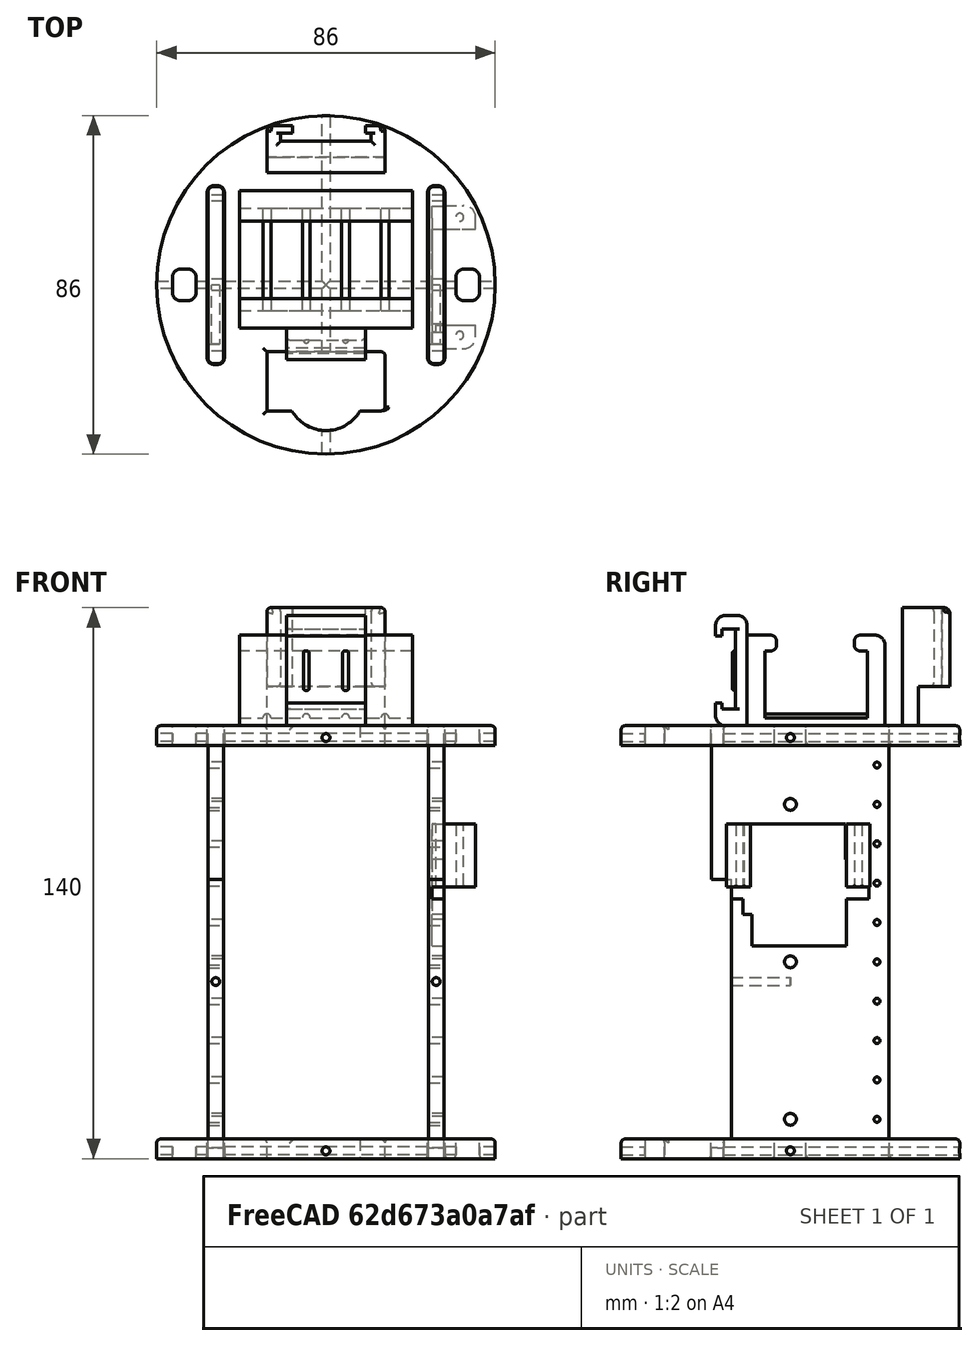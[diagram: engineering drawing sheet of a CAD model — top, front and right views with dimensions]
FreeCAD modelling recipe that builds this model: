
FCSTD DOCUMENT  (FreeCAD 1.0R39109 (Git))
Label: LateralIzquierdo_Capsula
License: All rights reserved
LicenseURL: http://en.wikipedia.org/wiki/All_rights_reserved
objects: Part::Cut×130, Part::Cylinder×98, Part::Fillet×96, Part::Box×72, Part::MultiFuse×37, Part::Offset×12, Part::Chamfer×1
note: 446 computed .brp shape members not serialized (recipe doc carries the construction recipe); baked Part::Feature solids carry a one-line shape summary decoded from their .brp

FEATURE [Part::Box] Box  label="Extensor"
  AttacherType = Attacher::AttachEngine3D
  Height = 66
  Length = 11
  Placement = pos=(30,-28,3) rot=(0,0,1;1.5708rad)
  Width = 60
FEATURE [Part::Box] Box001  label="Cubo001"
  AttacherType = Attacher::AttachEngine3D
  Height = 110
  Length = 45
  Placement = pos=(-30,25,0) rot=(0,0,-1;1.5708rad)
  Width = 4
FEATURE [Part::Box] Box002  label="Cubo002"
  AttacherType = Attacher::AttachEngine3D
  Height = 110
  Length = 45
  Placement = pos=(-30,25,0) rot=(0,0,-1;1.5708rad)
  Width = 4
FEATURE [Part::Box] Box003  label="Cubo003"
  AttacherType = Attacher::AttachEngine3D
  Height = 10
  Length = 30
  Placement = pos=(-15,-32,0) rot=(0,0,1;0rad)
  Width = 15
FEATURE [Part::Box] Box005  label="Cubo004"
  AttacherType = Attacher::AttachEngine3D
  Height = 15
  Length = 26
  Placement = pos=(-13,-23,110) rot=(0,0,1;0rad)
  Width = 35
FEATURE [Part::Box] Box006  label="Cubo005"
  AttacherType = Attacher::AttachEngine3D
  Height = 150
  Length = 6
  Width = 8
FEATURE [Part::Box] Box007  label="Cubo006"
  AttacherType = Attacher::AttachEngine3D
  Height = 150
  Length = 6
  Width = 8
FEATURE [Part::Box] Box008  label="Cubo007"
  AttacherType = Attacher::AttachEngine3D
  Height = 150
  Length = 6
  Width = 8
FEATURE [Part::Box] Box009  label="Cubo008"
  AttacherType = Attacher::AttachEngine3D
  Height = 150
  Length = 6
  Width = 8
FEATURE [Part::Box] Box010  label="Cubo009"
  AttacherType = Attacher::AttachEngine3D
  Height = 11.6
  Length = 20.8
  Placement = pos=(-10.5,-23,110) rot=(0,0,1;0rad)
  Width = 35
FEATURE [Part::Box] Box011  label="Cubo010"
  AttacherType = Attacher::AttachEngine3D
  Height = 11.6
  Length = 16
  Placement = pos=(-8,-23,116) rot=(0,0,1;0rad)
  Width = 35
FEATURE [Part::Box] Box095  label="Cubo095"
  AttacherType = Attacher::AttachEngine3D
  Height = 110
  Length = 45
  Placement = pos=(-30,25,0) rot=(0,0,-1;1.5708rad)
  Width = 4
FEATURE [Part::Box] Box096  label="Cubo096"
  AttacherType = Attacher::AttachEngine3D
  Height = 110
  Length = 45
  Placement = pos=(-30,25,0) rot=(0,0,-1;1.5708rad)
  Width = 4
FEATURE [Part::Box] Box097  label="Cubo097"
  AttacherType = Attacher::AttachEngine3D
  Height = 23
  Length = 24
  Width = 14
FEATURE [Part::Box] Box098  label="Cubo098"
  AttacherType = Attacher::AttachEngine3D
  Height = 3
  Length = 33.5
  Placement = pos=(-5,0,16) rot=(0,0,1;0rad)
  Width = 14
FEATURE [Part::Box] Box099  label="Cubo099"
  AttacherType = Attacher::AttachEngine3D
  Height = 1.4
  Length = 13
  Placement = pos=(9.8,5,28.6) rot=(0,0,1;0rad)
  Width = 4
FEATURE [Part::Box] Box100  label="Cubo100"
  AttacherType = Attacher::AttachEngine3D
  Height = 16
  Length = 10
  Placement = pos=(28,12.2,69) rot=(0,0,1;0rad)
  Width = 6
FEATURE [Part::Box] Box101  label="Cubo101"
  AttacherType = Attacher::AttachEngine3D
  Height = 16
  Length = 10
  Placement = pos=(28,-18.2,69) rot=(0,0,1;0rad)
  Width = 6
FEATURE [Part::Box] Box102  label="Extensor001"
  AttacherType = Attacher::AttachEngine3D
  Height = 66
  Length = 11
  Placement = pos=(30,-28,3) rot=(0,0,1;1.5708rad)
  Width = 60
FEATURE [Part::Box] Box104  label="Cubo102"
  AttacherType = Attacher::AttachEngine3D
  Height = 8
  Length = 20
  Width = 28
FEATURE [Part::Box] Box105  label="Cubo103"
  AttacherType = Attacher::AttachEngine3D
  Height = 2
  Length = 20.5
  Placement = pos=(0,4,4) rot=(0,0,1;0rad)
  Width = 20.5
FEATURE [Part::Box] Box106  label="Cubo104"
  AttacherType = Attacher::AttachEngine3D
  Height = 4
  Length = 20.5
  Placement = pos=(0,5,5) rot=(0,0,1;0rad)
  Width = 18.5
FEATURE [Part::Box] Box107  label="Cubo105"
  AttacherType = Attacher::AttachEngine3D
  Height = 8
  Length = 20
  Width = 30
FEATURE [Part::Box] Box108  label="Cubo106"
  AttacherType = Attacher::AttachEngine3D
  Height = 2
  Length = 20.5
  Placement = pos=(0,3.5,4) rot=(0,0,1;0rad)
  Width = 23
FEATURE [Part::Box] Box109  label="Cubo107"
  AttacherType = Attacher::AttachEngine3D
  Height = 4
  Length = 20.5
  Placement = pos=(0,5,5) rot=(0,0,1;0rad)
  Width = 18.5
FEATURE [Part::Box] Box110  label="Cubo108"
  AttacherType = Attacher::AttachEngine3D
  Height = 10
  Length = 20
  Placement = pos=(-9,-38,105) rot=(0,0,1;0rad)
  Width = 15
FEATURE [Part::Box] Box111  label="Cubo109"
  AttacherType = Attacher::AttachEngine3D
  Height = 110
  Length = 45
  Placement = pos=(-30,25,0) rot=(0,0,-1;1.5708rad)
  Width = 4
FEATURE [Part::Box] Box112  label="Extensor003"
  AttacherType = Attacher::AttachEngine3D
  Height = 66
  Length = 11
  Placement = pos=(30,-28,3) rot=(0,0,1;1.5708rad)
  Width = 60
FEATURE [Part::Box] Box113  label="Extensor004"
  AttacherType = Attacher::AttachEngine3D
  Height = 66
  Length = 11
  Placement = pos=(30,-28,3) rot=(0,0,1;1.5708rad)
  Width = 60
FEATURE [Part::Box] Box114  label="Cubo110"
  AttacherType = Attacher::AttachEngine3D
  Height = 110
  Length = 45
  Placement = pos=(-30,25,0) rot=(0,0,-1;1.5708rad)
  Width = 4
FEATURE [Part::Box] Box115  label="Cubo111"
  AttacherType = Attacher::AttachEngine3D
  Height = 23
  Length = 24
  Width = 14
FEATURE [Part::Box] Box116  label="Cubo112"
  AttacherType = Attacher::AttachEngine3D
  Height = 3
  Length = 33.5
  Placement = pos=(-5,0,16) rot=(0,0,1;0rad)
  Width = 14
FEATURE [Part::Box] Box117  label="Cubo113"
  AttacherType = Attacher::AttachEngine3D
  Height = 1.4
  Length = 13
  Placement = pos=(9.8,5,28.6) rot=(0,0,1;0rad)
  Width = 4
FEATURE [Part::Box] Box118  label="Cubo114"
  AttacherType = Attacher::AttachEngine3D
  Height = 16
  Length = 10
  Placement = pos=(28,12.2,69) rot=(0,0,1;0rad)
  Width = 6
FEATURE [Part::Box] Box119  label="Cubo115"
  AttacherType = Attacher::AttachEngine3D
  Height = 16
  Length = 10
  Placement = pos=(28,-18.2,69) rot=(0,0,1;0rad)
  Width = 6
FEATURE [Part::Box] Box120  label="Cubo116"
  AttacherType = Attacher::AttachEngine3D
  Height = 10
  Length = 4
  Placement = pos=(-30,-20,0) rot=(0,0,1;0rad)
  Width = 45
FEATURE [Part::Box] Box121  label="Cubo117"
  AttacherType = Attacher::AttachEngine3D
  Height = 10
  Length = 4
  Placement = pos=(-30,-20,0) rot=(0,0,1;0rad)
  Width = 45
FEATURE [Part::Box] Box122  label="Cubo118"
  AttacherType = Attacher::AttachEngine3D
  Height = 8
  Length = 20
  Width = 30
FEATURE [Part::Box] Box123  label="Cubo119"
  AttacherType = Attacher::AttachEngine3D
  Height = 2
  Length = 20.5
  Placement = pos=(0,3.5,4) rot=(0,0,1;0rad)
  Width = 23
FEATURE [Part::Box] Box124  label="Cubo120"
  AttacherType = Attacher::AttachEngine3D
  Height = 4
  Length = 20.5
  Placement = pos=(0,5,5) rot=(0,0,1;0rad)
  Width = 18.5
FEATURE [Part::Box] Box128  label="Cubo124"
  AttacherType = Attacher::AttachEngine3D
  Height = 30
  Length = 33
  Placement = pos=(-16,-43,115) rot=(0,0,1;0rad)
  Width = 30
FEATURE [Part::Box] Box129  label="Cubo125"
  AttacherType = Attacher::AttachEngine3D
  Height = 30
  Length = 33
  Placement = pos=(-16,13,110) rot=(0,0,1;0rad)
  Width = 30
FEATURE [Part::Box] Box130  label="Cubo126"
  AttacherType = Attacher::AttachEngine3D
  Height = 30
  Length = 30
  Placement = pos=(-16,13,110) rot=(0,0,1;0rad)
  Width = 4
FEATURE [Part::Box] Box131  label="Cubo127"
  AttacherType = Attacher::AttachEngine3D
  Height = 3.4
  Length = 21
  Placement = pos=(0,4.2,3) rot=(0,0,1;0rad)
  Width = 20.4
FEATURE [Part::Box] Box132  label="Cubo128"
  AttacherType = Attacher::AttachEngine3D
  Height = 4
  Length = 21
  Placement = pos=(0,5.75,6) rot=(0,0,1;0rad)
  Width = 17
FEATURE [Part::Box] Box133  label="Cubo129"
  AttacherType = Attacher::AttachEngine3D
  Height = 8
  Length = 20
  Width = 28
FEATURE [Part::Box] Box134  label="Cubo130"
  AttacherType = Attacher::AttachEngine3D
  Height = 16
  Length = 37
  Placement = pos=(-19,-15,110) rot=(0,0,1;0rad)
  Width = 30
FEATURE [Part::Box] Box135  label="Pila_ext"
  AttacherType = Attacher::AttachEngine3D
  Height = 25
  Length = 44
  Placement = pos=(-22,-11,110) rot=(0,0,1;0rad)
  Width = 35
FEATURE [Part::Box] Box136  label="Pila_int"
  AttacherType = Attacher::AttachEngine3D
  Height = 17
  Length = 44
  Placement = pos=(-22,-6.5,114) rot=(0,0,1;0rad)
  Width = 26
FEATURE [Part::Box] Box137  label="hueco_pila"
  AttacherType = Attacher::AttachEngine3D
  Height = 16.65
  Length = 44
  Placement = pos=(-22,-3.5,122) rot=(0,0,1;0rad)
  Width = 19.72
FEATURE [Part::Box] Box165  label="Cubo155"
  AttacherType = Attacher::AttachEngine3D
  Height = 17
  Length = 19
  Placement = pos=(27,-9.8,59) rot=(0,0,1;0rad)
  Width = 24
FEATURE [Part::Box] Box166  label="Cubo156"
  AttacherType = Attacher::AttachEngine3D
  Height = 66
  Length = 60
  Placement = pos=(-30,-20,5) rot=(0,0,1;0rad)
  Width = 5
FEATURE [Part::Box] Box167  label="Cubo157"
  AttacherType = Attacher::AttachEngine3D
  Height = 66
  Length = 60
  Placement = pos=(-30,-20,5) rot=(0,0,1;0rad)
  Width = 5
FEATURE [Part::Box] Box168  label="Cubo158"
  AttacherType = Attacher::AttachEngine3D
  Height = 3
  Length = 4
  Placement = pos=(27,7,66) rot=(0,0,1;0rad)
  Width = 13
FEATURE [Part::Box] Box169  label="Cubo159"
  AttacherType = Attacher::AttachEngine3D
  Height = 3
  Length = 4
  Placement = pos=(27,-9.8,56) rot=(0,0,1;0rad)
  Width = 24
FEATURE [Part::Box] Box170  label="Cubo160"
  AttacherType = Attacher::AttachEngine3D
  Height = 10
  Length = 30
  Placement = pos=(-15,-32,0) rot=(0,0,1;0rad)
  Width = 15
FEATURE [Part::Box] Box171  label="Cubo161"
  AttacherType = Attacher::AttachEngine3D
  Height = 150
  Length = 6
  Width = 8
FEATURE [Part::Box] Box172  label="Cubo162"
  AttacherType = Attacher::AttachEngine3D
  Height = 150
  Length = 6
  Width = 8
FEATURE [Part::Box] Box173  label="Cubo163"
  AttacherType = Attacher::AttachEngine3D
  Height = 110
  Length = 45
  Placement = pos=(-30,25,0) rot=(0,0,-1;1.5708rad)
  Width = 4
FEATURE [Part::Box] Box174  label="Extensor005"
  AttacherType = Attacher::AttachEngine3D
  Height = 66
  Length = 11
  Placement = pos=(30,-28,3) rot=(0,0,1;1.5708rad)
  Width = 60
FEATURE [Part::Box] Box175  label="Extensor006"
  AttacherType = Attacher::AttachEngine3D
  Height = 66
  Length = 11
  Placement = pos=(30,-28,3) rot=(0,0,1;1.5708rad)
  Width = 60
FEATURE [Part::Box] Box176  label="Cubo164"
  AttacherType = Attacher::AttachEngine3D
  Height = 110
  Length = 45
  Placement = pos=(-30,25,0) rot=(0,0,-1;1.5708rad)
  Width = 4
FEATURE [Part::Box] Box177  label="Cubo165"
  AttacherType = Attacher::AttachEngine3D
  Height = 23
  Length = 24
  Width = 14
FEATURE [Part::Box] Box178  label="Cubo166"
  AttacherType = Attacher::AttachEngine3D
  Height = 3
  Length = 33.5
  Placement = pos=(-5,0,16) rot=(0,0,1;0rad)
  Width = 14
FEATURE [Part::Box] Box179  label="Cubo167"
  AttacherType = Attacher::AttachEngine3D
  Height = 1.4
  Length = 13
  Placement = pos=(9.8,5,28.6) rot=(0,0,1;0rad)
  Width = 4
FEATURE [Part::Box] Box180  label="Cubo168"
  AttacherType = Attacher::AttachEngine3D
  Height = 16
  Length = 10
  Placement = pos=(28,12.2,69) rot=(0,0,1;0rad)
  Width = 6
FEATURE [Part::Box] Box181  label="Cubo169"
  AttacherType = Attacher::AttachEngine3D
  Height = 16
  Length = 10
  Placement = pos=(28,-18.2,69) rot=(0,0,1;0rad)
  Width = 6
FEATURE [Part::Box] Box182  label="Cubo170"
  AttacherType = Attacher::AttachEngine3D
  Height = 10
  Length = 4
  Placement = pos=(-30,-20,0) rot=(0,0,1;0rad)
  Width = 45
FEATURE [Part::Box] Box183  label="Cubo171"
  AttacherType = Attacher::AttachEngine3D
  Height = 10
  Length = 4
  Placement = pos=(-30,-20,0) rot=(0,0,1;0rad)
  Width = 45
FEATURE [Part::Box] Box184  label="Cubo172"
  AttacherType = Attacher::AttachEngine3D
  Height = 10
  Length = 120
  Placement = pos=(-50,-47,100) rot=(0,0,1;0rad)
  Width = 120
FEATURE [Part::Box] Box197  label="Cubo184"
  AttacherType = Attacher::AttachEngine3D
  Height = 16
  Length = 3
  Placement = pos=(27,12,69) rot=(0,0,1;0rad)
  Width = 2
FEATURE [Part::Box] Box198  label="Cubo185"
  AttacherType = Attacher::AttachEngine3D
  Height = 24
  Length = 3
  Placement = pos=(27,14.2,54) rot=(1,0,0;1.5708rad)
  Width = 4
FEATURE [Part::Cut] Cut016
  Base = -> Box005
  Tool = -> Box010
FEATURE [Part::Cut] Cut017
  Base = -> Cut016
  Placement = pos=(-5,0,0) rot=(0,0,1;1.5708rad)
  Tool = -> Box011
FEATURE [Part::Cut] Cut115
  Base = -> Box104
  Tool = -> Box105
FEATURE [Part::Cut] Cut116
  Base = -> Cut115
  Tool = -> Box106
FEATURE [Part::Cut] Cut117
  Base = -> Box107
  Tool = -> Box108
FEATURE [Part::Cut] Cut118
  Base = -> Cut117
  Tool = -> Box109
FEATURE [Part::Cut] Cut143
  Base = -> Box122
  Tool = -> Box123
FEATURE [Part::Cut] Cut144
  Base = -> Cut143
  Tool = -> Box124
FEATURE [Part::Cut] Cut149
  Base = -> Box133
  Tool = -> Box131
FEATURE [Part::Cut] Cut150
  Base = -> Cut149
  Tool = -> Box132
FEATURE [Part::Cut] Cut152
  Base = -> Box135
  Tool = -> Box136
FEATURE [Part::Cut] Cut153  label="PortaPIlas_9V"
  Base = -> Cut152
  Placement = pos=(0,0,-2) rot=(0,0,1;0rad)
  Tool = -> Box137
FEATURE [Part::Cylinder] Cylinder  label="Cilindro"
  Angle = 360
  AttacherType = Attacher::AttachEngine3D
  FirstAngle = 0
  Height = 5
  Radius = 43
  SecondAngle = 0
FEATURE [Part::Cylinder] Cylinder002  label="Cilindro002"
  Angle = 360
  AttacherType = Attacher::AttachEngine3D
  FirstAngle = 0
  Height = 20
  Placement = pos=(0,44,1.5) rot=(1,0,0;1.5708rad)
  Radius = 0.5
  SecondAngle = 0
FEATURE [Part::Cylinder] Cylinder003  label="Cilindro003"
  Angle = 360
  AttacherType = Attacher::AttachEngine3D
  FirstAngle = 0
  Height = 20
  Placement = pos=(0,-26,1.5) rot=(1,0,0;1.5708rad)
  Radius = 0.5
  SecondAngle = 0
FEATURE [Part::Cylinder] Cylinder004  label="Cilindro004"
  Angle = 360
  AttacherType = Attacher::AttachEngine3D
  FirstAngle = 0
  Height = 3
  Radius = 43
  SecondAngle = 0
FEATURE [Part::Cylinder] Cylinder005  label="Cilindro005"
  Angle = 360
  AttacherType = Attacher::AttachEngine3D
  FirstAngle = 0
  Height = 20
  Placement = pos=(0,44,1.5) rot=(1,0,0;1.5708rad)
  Radius = 0.5
  SecondAngle = 0
FEATURE [Part::Cylinder] Cylinder006  label="Cilindro006"
  Angle = 360
  AttacherType = Attacher::AttachEngine3D
  FirstAngle = 0
  Height = 20
  Placement = pos=(0,-26,1.5) rot=(1,0,0;1.5708rad)
  Radius = 0.5
  SecondAngle = 0
FEATURE [Part::Cylinder] Cylinder008  label="Cilindro008"
  Angle = 360
  AttacherType = Attacher::AttachEngine3D
  FirstAngle = 0
  Height = 100
  Placement = pos=(-46,0,50) rot=(0,1,0;1.5708rad)
  Radius = 1.5
  SecondAngle = 0
FEATURE [Part::Cylinder] Cylinder009  label="Cilindro009"
  Angle = 360
  AttacherType = Attacher::AttachEngine3D
  FirstAngle = 0
  Height = 100
  Placement = pos=(-46,0,90) rot=(0,1,0;1.5708rad)
  Radius = 1.5
  SecondAngle = 0
FEATURE [Part::Cylinder] Cylinder010  label="Cilindro010"
  Angle = 360
  AttacherType = Attacher::AttachEngine3D
  FirstAngle = 0
  Height = 100
  Placement = pos=(-46,0,10) rot=(0,1,0;1.5708rad)
  Radius = 1.5
  SecondAngle = 0
FEATURE [Part::Cylinder] Cylinder011  label="Cilindro011"
  Angle = 360
  AttacherType = Attacher::AttachEngine3D
  FirstAngle = 0
  Height = 10
  Placement = pos=(0,-27,0) rot=(0,0,1;0rad)
  Radius = 10
  SecondAngle = 0
FEATURE [Part::Cylinder] Cylinder071  label="Cilindro071"
  Angle = 360
  AttacherType = Attacher::AttachEngine3D
  FirstAngle = 0
  Height = 100
  Placement = pos=(-46,0,50) rot=(0,1,0;1.5708rad)
  Radius = 1.5
  SecondAngle = 0
FEATURE [Part::Cylinder] Cylinder072  label="Cilindro072"
  Angle = 360
  AttacherType = Attacher::AttachEngine3D
  FirstAngle = 0
  Height = 100
  Placement = pos=(-46,0,90) rot=(0,1,0;1.5708rad)
  Radius = 1.5
  SecondAngle = 0
FEATURE [Part::Cylinder] Cylinder073  label="Cilindro073"
  Angle = 360
  AttacherType = Attacher::AttachEngine3D
  FirstAngle = 0
  Height = 100
  Placement = pos=(-46,0,10) rot=(0,1,0;1.5708rad)
  Radius = 1.5
  SecondAngle = 0
FEATURE [Part::Cylinder] Cylinder074  label="Cilindro074"
  Angle = 360
  AttacherType = Attacher::AttachEngine3D
  FirstAngle = 0
  Height = 3
  Placement = pos=(7,7,23) rot=(0,0,1;0rad)
  Radius = 7
  SecondAngle = 0
FEATURE [Part::Cylinder] Cylinder075  label="Cilindro075"
  Angle = 360
  AttacherType = Attacher::AttachEngine3D
  FirstAngle = 0
  Height = 3
  Placement = pos=(14,7,23) rot=(0,0,1;0rad)
  Radius = 2
  SecondAngle = 0
FEATURE [Part::Cylinder] Cylinder076  label="Cilindro076"
  Angle = 360
  AttacherType = Attacher::AttachEngine3D
  FirstAngle = 0
  Height = 10
  Placement = pos=(-3.2,7,12) rot=(0,0,1;0rad)
  Radius = 1.65
  SecondAngle = 0
FEATURE [Part::Cylinder] Cylinder077  label="Cilindro077"
  Angle = 360
  AttacherType = Attacher::AttachEngine3D
  FirstAngle = 0
  Height = 10
  Placement = pos=(26.8,7,12) rot=(0,0,1;0rad)
  Radius = 1.65
  SecondAngle = 0
FEATURE [Part::Cylinder] Cylinder078  label="Cilindro078"
  Angle = 360
  AttacherType = Attacher::AttachEngine3D
  FirstAngle = 0
  Height = 4
  Placement = pos=(7,7,26) rot=(0,0,1;0rad)
  Radius = 3.5
  SecondAngle = 0
FEATURE [Part::Cylinder] Cylinder079  label="Cilindro079"
  Angle = 360
  AttacherType = Attacher::AttachEngine3D
  FirstAngle = 0
  Height = 10
  Placement = pos=(21,7,25) rot=(0,0,1;0rad)
  Radius = 0.25
  SecondAngle = 0
FEATURE [Part::Cylinder] Cylinder080  label="Cilindro080"
  Angle = 360
  AttacherType = Attacher::AttachEngine3D
  FirstAngle = 0
  Height = 10
  Placement = pos=(19,7,25) rot=(0,0,1;0rad)
  Radius = 0.25
  SecondAngle = 0
FEATURE [Part::Cylinder] Cylinder081  label="Cilindro081"
  Angle = 360
  AttacherType = Attacher::AttachEngine3D
  FirstAngle = 0
  Height = 10
  Placement = pos=(17,7,25) rot=(0,0,1;0rad)
  Radius = 0.25
  SecondAngle = 0
FEATURE [Part::Cylinder] Cylinder082  label="Cilindro082"
  Angle = 360
  AttacherType = Attacher::AttachEngine3D
  FirstAngle = 0
  Height = 10
  Placement = pos=(15,7,27) rot=(0,0,1;0rad)
  Radius = 0.25
  SecondAngle = 0
FEATURE [Part::Cylinder] Cylinder083  label="Cilindro083"
  Angle = 360
  AttacherType = Attacher::AttachEngine3D
  FirstAngle = 0
  Height = 10
  Placement = pos=(13,7,27) rot=(0,0,1;0rad)
  Radius = 0.25
  SecondAngle = 0
FEATURE [Part::Cylinder] Cylinder084  label="Cilindro084"
  Angle = 360
  AttacherType = Attacher::AttachEngine3D
  FirstAngle = 0
  Height = 20
  Placement = pos=(34,-14.8,66) rot=(0,0,1;0rad)
  Radius = 1
  SecondAngle = 0
FEATURE [Part::Cylinder] Cylinder085  label="Cilindro085"
  Angle = 360
  AttacherType = Attacher::AttachEngine3D
  FirstAngle = 0
  Height = 20
  Placement = pos=(34,15.2,66) rot=(0,0,1;0rad)
  Radius = 1
  SecondAngle = 0
FEATURE [Part::Cylinder] Cylinder086  label="Cilindro086"
  Angle = 360
  AttacherType = Attacher::AttachEngine3D
  FirstAngle = 0
  Height = 100
  Placement = pos=(-46,0,50) rot=(0,1,0;1.5708rad)
  Radius = 1.5
  SecondAngle = 0
FEATURE [Part::Cylinder] Cylinder087  label="Cilindro087"
  Angle = 360
  AttacherType = Attacher::AttachEngine3D
  FirstAngle = 0
  Height = 100
  Placement = pos=(-46,0,90) rot=(0,1,0;1.5708rad)
  Radius = 1.5
  SecondAngle = 0
FEATURE [Part::Cylinder] Cylinder088  label="Cilindro088"
  Angle = 360
  AttacherType = Attacher::AttachEngine3D
  FirstAngle = 0
  Height = 100
  Placement = pos=(-46,0,10) rot=(0,1,0;1.5708rad)
  Radius = 1.5
  SecondAngle = 0
FEATURE [Part::Cylinder] Cylinder089  label="Cilindro089"
  Angle = 360
  AttacherType = Attacher::AttachEngine3D
  FirstAngle = 0
  Height = 100
  Placement = pos=(-46,0,50) rot=(0,1,0;1.5708rad)
  Radius = 1.5
  SecondAngle = 0
FEATURE [Part::Cylinder] Cylinder090  label="Cilindro090"
  Angle = 360
  AttacherType = Attacher::AttachEngine3D
  FirstAngle = 0
  Height = 100
  Placement = pos=(-46,0,90) rot=(0,1,0;1.5708rad)
  Radius = 1.5
  SecondAngle = 0
FEATURE [Part::Cylinder] Cylinder091  label="Cilindro091"
  Angle = 360
  AttacherType = Attacher::AttachEngine3D
  FirstAngle = 0
  Height = 100
  Placement = pos=(-46,0,10) rot=(0,1,0;1.5708rad)
  Radius = 1.5
  SecondAngle = 0
FEATURE [Part::Cylinder] Cylinder092  label="Cilindro092"
  Angle = 360
  AttacherType = Attacher::AttachEngine3D
  FirstAngle = 0
  Height = 3
  Placement = pos=(7,7,23) rot=(0,0,1;0rad)
  Radius = 7
  SecondAngle = 0
FEATURE [Part::Cylinder] Cylinder093  label="Cilindro093"
  Angle = 360
  AttacherType = Attacher::AttachEngine3D
  FirstAngle = 0
  Height = 3
  Placement = pos=(14,7,23) rot=(0,0,1;0rad)
  Radius = 2
  SecondAngle = 0
FEATURE [Part::Cylinder] Cylinder094  label="Cilindro094"
  Angle = 360
  AttacherType = Attacher::AttachEngine3D
  FirstAngle = 0
  Height = 10
  Placement = pos=(-3.2,7,12) rot=(0,0,1;0rad)
  Radius = 1.65
  SecondAngle = 0
FEATURE [Part::Cylinder] Cylinder095  label="Cilindro095"
  Angle = 360
  AttacherType = Attacher::AttachEngine3D
  FirstAngle = 0
  Height = 10
  Placement = pos=(26.8,7,12) rot=(0,0,1;0rad)
  Radius = 1.65
  SecondAngle = 0
FEATURE [Part::Cylinder] Cylinder096  label="Cilindro096"
  Angle = 360
  AttacherType = Attacher::AttachEngine3D
  FirstAngle = 0
  Height = 4
  Placement = pos=(7,7,26) rot=(0,0,1;0rad)
  Radius = 3.5
  SecondAngle = 0
FEATURE [Part::Cylinder] Cylinder097  label="Cilindro097"
  Angle = 360
  AttacherType = Attacher::AttachEngine3D
  FirstAngle = 0
  Height = 10
  Placement = pos=(21,7,25) rot=(0,0,1;0rad)
  Radius = 0.25
  SecondAngle = 0
FEATURE [Part::Cylinder] Cylinder098  label="Cilindro098"
  Angle = 360
  AttacherType = Attacher::AttachEngine3D
  FirstAngle = 0
  Height = 10
  Placement = pos=(19,7,25) rot=(0,0,1;0rad)
  Radius = 0.25
  SecondAngle = 0
FEATURE [Part::Cylinder] Cylinder099  label="Cilindro099"
  Angle = 360
  AttacherType = Attacher::AttachEngine3D
  FirstAngle = 0
  Height = 10
  Placement = pos=(17,7,25) rot=(0,0,1;0rad)
  Radius = 0.25
  SecondAngle = 0
FEATURE [Part::Cylinder] Cylinder100  label="Cilindro100"
  Angle = 360
  AttacherType = Attacher::AttachEngine3D
  FirstAngle = 0
  Height = 10
  Placement = pos=(15,7,27) rot=(0,0,1;0rad)
  Radius = 0.25
  SecondAngle = 0
FEATURE [Part::Cylinder] Cylinder101  label="Cilindro101"
  Angle = 360
  AttacherType = Attacher::AttachEngine3D
  FirstAngle = 0
  Height = 10
  Placement = pos=(13,7,27) rot=(0,0,1;0rad)
  Radius = 0.25
  SecondAngle = 0
FEATURE [Part::Cylinder] Cylinder102  label="Cilindro102"
  Angle = 360
  AttacherType = Attacher::AttachEngine3D
  FirstAngle = 0
  Height = 20
  Placement = pos=(34,-14.8,66) rot=(0,0,1;0rad)
  Radius = 1
  SecondAngle = 0
FEATURE [Part::Cylinder] Cylinder103  label="Cilindro103"
  Angle = 360
  AttacherType = Attacher::AttachEngine3D
  FirstAngle = 0
  Height = 20
  Placement = pos=(34,15.2,66) rot=(0,0,1;0rad)
  Radius = 1
  SecondAngle = 0
FEATURE [Part::Cylinder] Cylinder104  label="Cilindro104"
  Angle = 360
  AttacherType = Attacher::AttachEngine3D
  FirstAngle = 0
  Height = 100
  Placement = pos=(0,52,2) rot=(1,0,0;1.5708rad)
  Radius = 1
  SecondAngle = 0
FEATURE [Part::Cylinder] Cylinder109  label="Cilindro109"
  Angle = 360
  AttacherType = Attacher::AttachEngine3D
  FirstAngle = 0
  Height = 15
  Placement = pos=(-28,0,45) rot=(1,0,0;1.5708rad)
  Radius = 1
  SecondAngle = 0
FEATURE [Part::Cylinder] Cylinder110  label="Cilindro110"
  Angle = 360
  AttacherType = Attacher::AttachEngine3D
  FirstAngle = 0
  Height = 15
  Placement = pos=(28,0,45) rot=(1,0,0;1.5708rad)
  Radius = 1
  SecondAngle = 0
FEATURE [Part::Cylinder] Cylinder111  label="Cilindro111"
  Angle = 360
  AttacherType = Attacher::AttachEngine3D
  FirstAngle = 0
  Height = 67
  Placement = pos=(-33,22,10) rot=(0,1,0;1.5708rad)
  Radius = 0.75
  SecondAngle = 0
FEATURE [Part::Cylinder] Cylinder112  label="Cilindro112"
  Angle = 360
  AttacherType = Attacher::AttachEngine3D
  FirstAngle = 0
  Height = 67
  Placement = pos=(-33,22,100) rot=(0,1,0;1.5708rad)
  Radius = 0.75
  SecondAngle = 0
FEATURE [Part::Cylinder] Cylinder113  label="Cilindro113"
  Angle = 360
  AttacherType = Attacher::AttachEngine3D
  FirstAngle = 0
  Height = 67
  Placement = pos=(-33,22,20) rot=(0,1,0;1.5708rad)
  Radius = 0.75
  SecondAngle = 0
FEATURE [Part::Cylinder] Cylinder114  label="Cilindro114"
  Angle = 360
  AttacherType = Attacher::AttachEngine3D
  FirstAngle = 0
  Height = 67
  Placement = pos=(-33,22,30) rot=(0,1,0;1.5708rad)
  Radius = 0.75
  SecondAngle = 0
FEATURE [Part::Cylinder] Cylinder115  label="Cilindro115"
  Angle = 360
  AttacherType = Attacher::AttachEngine3D
  FirstAngle = 0
  Height = 67
  Placement = pos=(-33,22,40) rot=(0,1,0;1.5708rad)
  Radius = 0.75
  SecondAngle = 0
FEATURE [Part::Cylinder] Cylinder116  label="Cilindro116"
  Angle = 360
  AttacherType = Attacher::AttachEngine3D
  FirstAngle = 0
  Height = 67
  Placement = pos=(-33,22,50) rot=(0,1,0;1.5708rad)
  Radius = 0.75
  SecondAngle = 0
FEATURE [Part::Cylinder] Cylinder117  label="Cilindro117"
  Angle = 360
  AttacherType = Attacher::AttachEngine3D
  FirstAngle = 0
  Height = 67
  Placement = pos=(-33,22,60) rot=(0,1,0;1.5708rad)
  Radius = 0.75
  SecondAngle = 0
FEATURE [Part::Cylinder] Cylinder118  label="Cilindro118"
  Angle = 360
  AttacherType = Attacher::AttachEngine3D
  FirstAngle = 0
  Height = 67
  Placement = pos=(-33,22,70) rot=(0,1,0;1.5708rad)
  Radius = 0.75
  SecondAngle = 0
FEATURE [Part::Cylinder] Cylinder119  label="Cilindro119"
  Angle = 360
  AttacherType = Attacher::AttachEngine3D
  FirstAngle = 0
  Height = 67
  Placement = pos=(-33,22,80) rot=(0,1,0;1.5708rad)
  Radius = 0.75
  SecondAngle = 0
FEATURE [Part::Cylinder] Cylinder120  label="Cilindro120"
  Angle = 360
  AttacherType = Attacher::AttachEngine3D
  FirstAngle = 0
  Height = 67
  Placement = pos=(-33,22,90) rot=(0,1,0;1.5708rad)
  Radius = 0.75
  SecondAngle = 0
FEATURE [Part::Cylinder] Cylinder121  label="Cilindro121"
  Angle = 360
  AttacherType = Attacher::AttachEngine3D
  FirstAngle = 0
  Height = 67
  Placement = pos=(-33,22,10) rot=(0,1,0;1.5708rad)
  Radius = 0.75
  SecondAngle = 0
FEATURE [Part::Cylinder] Cylinder122  label="Cilindro122"
  Angle = 360
  AttacherType = Attacher::AttachEngine3D
  FirstAngle = 0
  Height = 67
  Placement = pos=(-33,22,100) rot=(0,1,0;1.5708rad)
  Radius = 0.75
  SecondAngle = 0
FEATURE [Part::Cylinder] Cylinder123  label="Cilindro123"
  Angle = 360
  AttacherType = Attacher::AttachEngine3D
  FirstAngle = 0
  Height = 67
  Placement = pos=(-33,22,20) rot=(0,1,0;1.5708rad)
  Radius = 0.75
  SecondAngle = 0
FEATURE [Part::Cylinder] Cylinder124  label="Cilindro124"
  Angle = 360
  AttacherType = Attacher::AttachEngine3D
  FirstAngle = 0
  Height = 67
  Placement = pos=(-33,22,30) rot=(0,1,0;1.5708rad)
  Radius = 0.75
  SecondAngle = 0
FEATURE [Part::Cylinder] Cylinder125  label="Cilindro125"
  Angle = 360
  AttacherType = Attacher::AttachEngine3D
  FirstAngle = 0
  Height = 67
  Placement = pos=(-33,22,40) rot=(0,1,0;1.5708rad)
  Radius = 0.75
  SecondAngle = 0
FEATURE [Part::Cylinder] Cylinder126  label="Cilindro126"
  Angle = 360
  AttacherType = Attacher::AttachEngine3D
  FirstAngle = 0
  Height = 67
  Placement = pos=(-33,22,50) rot=(0,1,0;1.5708rad)
  Radius = 0.75
  SecondAngle = 0
FEATURE [Part::Cylinder] Cylinder127  label="Cilindro127"
  Angle = 360
  AttacherType = Attacher::AttachEngine3D
  FirstAngle = 0
  Height = 67
  Placement = pos=(-33,22,60) rot=(0,1,0;1.5708rad)
  Radius = 0.75
  SecondAngle = 0
FEATURE [Part::Cylinder] Cylinder128  label="Cilindro128"
  Angle = 360
  AttacherType = Attacher::AttachEngine3D
  FirstAngle = 0
  Height = 67
  Placement = pos=(-33,22,70) rot=(0,1,0;1.5708rad)
  Radius = 0.75
  SecondAngle = 0
FEATURE [Part::Cylinder] Cylinder129  label="Cilindro129"
  Angle = 360
  AttacherType = Attacher::AttachEngine3D
  FirstAngle = 0
  Height = 67
  Placement = pos=(-33,22,80) rot=(0,1,0;1.5708rad)
  Radius = 0.75
  SecondAngle = 0
FEATURE [Part::Cylinder] Cylinder130  label="Cilindro130"
  Angle = 360
  AttacherType = Attacher::AttachEngine3D
  FirstAngle = 0
  Height = 67
  Placement = pos=(-33,22,90) rot=(0,1,0;1.5708rad)
  Radius = 0.75
  SecondAngle = 0
FEATURE [Part::Cylinder] Cylinder131  label="Cilindro131"
  Angle = 360
  AttacherType = Attacher::AttachEngine3D
  FirstAngle = 0
  Height = 67
  Placement = pos=(-33,22,70) rot=(0,1,0;1.5708rad)
  Radius = 0.75
  SecondAngle = 0
FEATURE [Part::Cylinder] Cylinder133  label="Cilindro133"
  Angle = 360
  AttacherType = Attacher::AttachEngine3D
  FirstAngle = 0
  Height = 110
  Placement = pos=(-55,0,2) rot=(0.57735,0.57735,0.57735;2.0944rad)
  Radius = 1
  SecondAngle = 0
FEATURE [Part::Cylinder] Cylinder134  label="Cilindro134"
  Angle = 360
  AttacherType = Attacher::AttachEngine3D
  FirstAngle = 0
  Height = 5
  Radius = 43
  SecondAngle = 0
FEATURE [Part::Cylinder] Cylinder135  label="Cilindro135"
  Angle = 360
  AttacherType = Attacher::AttachEngine3D
  FirstAngle = 0
  Height = 20
  Placement = pos=(0,44,1.5) rot=(1,0,0;1.5708rad)
  Radius = 0.5
  SecondAngle = 0
FEATURE [Part::Cylinder] Cylinder136  label="Cilindro136"
  Angle = 360
  AttacherType = Attacher::AttachEngine3D
  FirstAngle = 0
  Height = 20
  Placement = pos=(0,-26,1.5) rot=(1,0,0;1.5708rad)
  Radius = 0.5
  SecondAngle = 0
FEATURE [Part::Cylinder] Cylinder137  label="Cilindro137"
  Angle = 360
  AttacherType = Attacher::AttachEngine3D
  FirstAngle = 0
  Height = 10
  Placement = pos=(0,-27,0) rot=(0,0,1;0rad)
  Radius = 10
  SecondAngle = 0
FEATURE [Part::Cylinder] Cylinder138  label="Cilindro138"
  Angle = 360
  AttacherType = Attacher::AttachEngine3D
  FirstAngle = 0
  Height = 100
  Placement = pos=(-46,0,50) rot=(0,1,0;1.5708rad)
  Radius = 1.5
  SecondAngle = 0
FEATURE [Part::Cylinder] Cylinder139  label="Cilindro139"
  Angle = 360
  AttacherType = Attacher::AttachEngine3D
  FirstAngle = 0
  Height = 100
  Placement = pos=(-46,0,90) rot=(0,1,0;1.5708rad)
  Radius = 1.5
  SecondAngle = 0
FEATURE [Part::Cylinder] Cylinder140  label="Cilindro140"
  Angle = 360
  AttacherType = Attacher::AttachEngine3D
  FirstAngle = 0
  Height = 100
  Placement = pos=(-46,0,10) rot=(0,1,0;1.5708rad)
  Radius = 1.5
  SecondAngle = 0
FEATURE [Part::Cylinder] Cylinder141  label="Cilindro141"
  Angle = 360
  AttacherType = Attacher::AttachEngine3D
  FirstAngle = 0
  Height = 100
  Placement = pos=(-46,0,50) rot=(0,1,0;1.5708rad)
  Radius = 1.5
  SecondAngle = 0
FEATURE [Part::Cylinder] Cylinder142  label="Cilindro142"
  Angle = 360
  AttacherType = Attacher::AttachEngine3D
  FirstAngle = 0
  Height = 100
  Placement = pos=(-46,0,90) rot=(0,1,0;1.5708rad)
  Radius = 1.5
  SecondAngle = 0
FEATURE [Part::Cylinder] Cylinder143  label="Cilindro143"
  Angle = 360
  AttacherType = Attacher::AttachEngine3D
  FirstAngle = 0
  Height = 100
  Placement = pos=(-46,0,10) rot=(0,1,0;1.5708rad)
  Radius = 1.5
  SecondAngle = 0
FEATURE [Part::Cylinder] Cylinder144  label="Cilindro144"
  Angle = 360
  AttacherType = Attacher::AttachEngine3D
  FirstAngle = 0
  Height = 3
  Placement = pos=(7,7,23) rot=(0,0,1;0rad)
  Radius = 7
  SecondAngle = 0
FEATURE [Part::Cylinder] Cylinder145  label="Cilindro145"
  Angle = 360
  AttacherType = Attacher::AttachEngine3D
  FirstAngle = 0
  Height = 3
  Placement = pos=(14,7,23) rot=(0,0,1;0rad)
  Radius = 2
  SecondAngle = 0
FEATURE [Part::Cylinder] Cylinder146  label="Cilindro146"
  Angle = 360
  AttacherType = Attacher::AttachEngine3D
  FirstAngle = 0
  Height = 10
  Placement = pos=(-3.2,7,12) rot=(0,0,1;0rad)
  Radius = 1.65
  SecondAngle = 0
FEATURE [Part::Cylinder] Cylinder147  label="Cilindro147"
  Angle = 360
  AttacherType = Attacher::AttachEngine3D
  FirstAngle = 0
  Height = 10
  Placement = pos=(26.8,7,12) rot=(0,0,1;0rad)
  Radius = 1.65
  SecondAngle = 0
FEATURE [Part::Cylinder] Cylinder148  label="Cilindro148"
  Angle = 360
  AttacherType = Attacher::AttachEngine3D
  FirstAngle = 0
  Height = 4
  Placement = pos=(7,7,26) rot=(0,0,1;0rad)
  Radius = 3.5
  SecondAngle = 0
FEATURE [Part::Cylinder] Cylinder149  label="Cilindro149"
  Angle = 360
  AttacherType = Attacher::AttachEngine3D
  FirstAngle = 0
  Height = 10
  Placement = pos=(21,7,25) rot=(0,0,1;0rad)
  Radius = 0.25
  SecondAngle = 0
FEATURE [Part::Cylinder] Cylinder150  label="Cilindro150"
  Angle = 360
  AttacherType = Attacher::AttachEngine3D
  FirstAngle = 0
  Height = 10
  Placement = pos=(19,7,25) rot=(0,0,1;0rad)
  Radius = 0.25
  SecondAngle = 0
FEATURE [Part::Cylinder] Cylinder151  label="Cilindro151"
  Angle = 360
  AttacherType = Attacher::AttachEngine3D
  FirstAngle = 0
  Height = 10
  Placement = pos=(17,7,25) rot=(0,0,1;0rad)
  Radius = 0.25
  SecondAngle = 0
FEATURE [Part::Cylinder] Cylinder152  label="Cilindro152"
  Angle = 360
  AttacherType = Attacher::AttachEngine3D
  FirstAngle = 0
  Height = 10
  Placement = pos=(15,7,27) rot=(0,0,1;0rad)
  Radius = 0.25
  SecondAngle = 0
FEATURE [Part::Cylinder] Cylinder153  label="Cilindro153"
  Angle = 360
  AttacherType = Attacher::AttachEngine3D
  FirstAngle = 0
  Height = 10
  Placement = pos=(13,7,27) rot=(0,0,1;0rad)
  Radius = 0.25
  SecondAngle = 0
FEATURE [Part::Cylinder] Cylinder154  label="Cilindro154"
  Angle = 360
  AttacherType = Attacher::AttachEngine3D
  FirstAngle = 0
  Height = 20
  Placement = pos=(34,-14.8,66) rot=(0,0,1;0rad)
  Radius = 1
  SecondAngle = 0
FEATURE [Part::Cylinder] Cylinder155  label="Cilindro155"
  Angle = 360
  AttacherType = Attacher::AttachEngine3D
  FirstAngle = 0
  Height = 20
  Placement = pos=(34,15.2,66) rot=(0,0,1;0rad)
  Radius = 1
  SecondAngle = 0
FEATURE [Part::Cylinder] Cylinder156  label="Cilindro156"
  Angle = 360
  AttacherType = Attacher::AttachEngine3D
  FirstAngle = 0
  Height = 100
  Placement = pos=(0,52,2) rot=(1,0,0;1.5708rad)
  Radius = 1
  SecondAngle = 0
FEATURE [Part::Cylinder] Cylinder157  label="Cilindro157"
  Angle = 360
  AttacherType = Attacher::AttachEngine3D
  FirstAngle = 0
  Height = 110
  Placement = pos=(-55,0,2) rot=(0.57735,0.57735,0.57735;2.0944rad)
  Radius = 1
  SecondAngle = 0
FEATURE [Part::Cylinder] Cylinder158  label="Cilindro158"
  Angle = 360
  AttacherType = Attacher::AttachEngine3D
  FirstAngle = 0
  Height = 29
  Placement = pos=(-15,22,112) rot=(1,0,0;1.5708rad)
  Radius = 1
  SecondAngle = 0
FEATURE [Part::Cylinder] Cylinder159  label="Cilindro159"
  Angle = 360
  AttacherType = Attacher::AttachEngine3D
  FirstAngle = 0
  Height = 29
  Placement = pos=(-5,22,112) rot=(1,0,0;1.5708rad)
  Radius = 1
  SecondAngle = 0
FEATURE [Part::Cylinder] Cylinder160  label="Cilindro160"
  Angle = 360
  AttacherType = Attacher::AttachEngine3D
  FirstAngle = 0
  Height = 29
  Placement = pos=(5,22,112) rot=(1,0,0;1.5708rad)
  Radius = 1
  SecondAngle = 0
FEATURE [Part::Cylinder] Cylinder161  label="Cilindro161"
  Angle = 360
  AttacherType = Attacher::AttachEngine3D
  FirstAngle = 0
  Height = 29
  Placement = pos=(15,22,112) rot=(1,0,0;1.5708rad)
  Radius = 1
  SecondAngle = 0
FEATURE [Part::Cylinder] Cylinder162  label="Cilindro162"
  Angle = 360
  AttacherType = Attacher::AttachEngine3D
  FirstAngle = 0
  Height = 10
  Placement = pos=(-5,-14,119) rot=(0,0,1;0rad)
  Radius = 0.75
  SecondAngle = 0
FEATURE [Part::Cylinder] Cylinder163  label="Cilindro163"
  Angle = 360
  AttacherType = Attacher::AttachEngine3D
  FirstAngle = 0
  Height = 10
  Placement = pos=(5,-14,119) rot=(0,0,1;0rad)
  Radius = 0.75
  SecondAngle = 0
FEATURE [Part::Fillet] Fillet
  Base = -> Cylinder
  EdgeLinks = -> Cylinder [Edge3]
  Edges = 1 edges r=1: [Edge3]
FEATURE [Part::Cut] Cut
  Base = -> Fillet
  Tool = -> Cylinder003
FEATURE [Part::Cut] Cut001  label="BaseInf"
  Base = -> Cut
  Tool = -> Cylinder002
FEATURE [Part::Cut] Cut093  label="BaseInf001"
  Base = -> Cut001
  Tool = -> Cylinder011
FEATURE [Part::Cut] Cut094  label="BaseInf002"
  Base = -> Cut093
  Tool = -> Box003
FEATURE [Part::Fillet] Fillet003
  Base = -> Cut118
  EdgeLinks = -> Cut118 [Edge23]
  Edges = 1 edges r=1: [Edge23]
FEATURE [Part::Fillet] Fillet004
  Base = -> Fillet003
  EdgeLinks = -> Fillet003 [Edge4]
  Edges = 1 edges r=1: [Edge4]
FEATURE [Part::Fillet] Fillet005  label="PortaSensor_Inclinacion001"
  Base = -> Fillet004
  EdgeLinks = -> Fillet004 [Edge34]
  Edges = 1 edges r=1: [Edge34]
  Placement = pos=(0,3.5,4) rot=(0,0,1;0rad)
FEATURE [Part::Fillet] Fillet006
  Base = -> Fillet005
  EdgeLinks = -> Fillet005 [Edge48]
  Edges = 1 edges r=1: [Edge48]
FEATURE [Part::Fillet] Fillet007  label="PortaSensor_TemHum"
  Base = -> Fillet006
  EdgeLinks = -> Fillet006 [Edge7,Edge18]
  Edges = 2 edges r=1: [Edge7,Edge18]
  Placement = pos=(-18,-9,137) rot=(0.57735,0.57735,-0.57735;2.0944rad)
FEATURE [Part::Fillet] Fillet009
  Base = -> Cylinder004
  EdgeLinks = -> Cylinder004 [Edge3]
  Edges = 1 edges r=1: [Edge3]
FEATURE [Part::Cut] Cut002
  Base = -> Fillet009
  Tool = -> Cylinder006
FEATURE [Part::Cut] Cut003
  Base = -> Cut002
  Placement = pos=(0,0,97) rot=(0,0,1;0rad)
  Tool = -> Cylinder005
FEATURE [Part::Fillet] Fillet010
  Base = -> Box001
  EdgeLinks = -> Box001 [Edge1,Edge3]
  Edges = 2 edges r=1.5: [Edge1,Edge3]
FEATURE [Part::Fillet] Fillet011  label="Lateral_Iz"
  Base = -> Fillet010
  EdgeLinks = -> Fillet010 [Edge17,Edge18]
  Edges = 2 edges r=1.5: [Edge17,Edge18]
FEATURE [Part::Fillet] Fillet012
  Base = -> Box002
  EdgeLinks = -> Box002 [Edge1,Edge3]
  Edges = 2 edges r=1.5: [Edge1,Edge3]
FEATURE [Part::Fillet] Fillet013  label="Lateral_De"
  Base = -> Fillet012
  EdgeLinks = -> Fillet012 [Edge17,Edge18]
  Edges = 2 edges r=1.5: [Edge17,Edge18]
  Placement = pos=(56,0,0) rot=(0,0,1;0rad)
FEATURE [Part::Fillet] Fillet019
  Base = -> Box006
  EdgeLinks = -> Box006 [Edge1,Edge3,Edge5,Edge7]
  Edges = 4 edges r=2: [Edge1,Edge3,Edge5,Edge7]
  Placement = pos=(-39,-4,0) rot=(0,0,1;0rad)
FEATURE [Part::Fillet] Fillet020
  Base = -> Box007
  EdgeLinks = -> Box007 [Edge1,Edge3,Edge5,Edge7]
  Edges = 4 edges r=2: [Edge1,Edge3,Edge5,Edge7]
  Placement = pos=(33,-4,0) rot=(0,0,1;0rad)
FEATURE [Part::Fillet] Fillet021
  Base = -> Box008
  EdgeLinks = -> Box008 [Edge1,Edge3,Edge5,Edge7]
  Edges = 4 edges r=2: [Edge1,Edge3,Edge5,Edge7]
  Placement = pos=(-39,-4,0) rot=(0,0,1;0rad)
FEATURE [Part::Cut] Cut095
  Base = -> Cut094
  Tool = -> Fillet021
FEATURE [Part::Cut] Cut096  label="BaseInf003"
  Base = -> Cut095
  Tool = -> Fillet020
FEATURE [Part::Fillet] Fillet022
  Base = -> Box009
  EdgeLinks = -> Box009 [Edge1,Edge3,Edge5,Edge7]
  Edges = 4 edges r=2: [Edge1,Edge3,Edge5,Edge7]
  Placement = pos=(33,-4,0) rot=(0,0,1;0rad)
FEATURE [Part::Fillet] Fillet032
  Base = -> Box095
  EdgeLinks = -> Box095 [Edge1,Edge3]
  Edges = 2 edges r=1.5: [Edge1,Edge3]
FEATURE [Part::Fillet] Fillet033  label="Lateral_De001"
  Base = -> Fillet032
  EdgeLinks = -> Fillet032 [Edge17,Edge18]
  Edges = 2 edges r=1.5: [Edge17,Edge18]
  Placement = pos=(56,0,0) rot=(0,0,1;0rad)
FEATURE [Part::Cut] Cut100
  Base = -> Fillet033
  Tool = -> Cylinder010
FEATURE [Part::Cut] Cut101
  Base = -> Cut100
  Tool = -> Cylinder009
FEATURE [Part::Cut] Cut102
  Base = -> Cut101
  Tool = -> Cylinder008
FEATURE [Part::Fillet] Fillet034
  Base = -> Box096
  EdgeLinks = -> Box096 [Edge1,Edge3]
  Edges = 2 edges r=1.5: [Edge1,Edge3]
FEATURE [Part::Fillet] Fillet035  label="Lateral_Iz001"
  Base = -> Fillet034
  EdgeLinks = -> Fillet034 [Edge17,Edge18]
  Edges = 2 edges r=1.5: [Edge17,Edge18]
FEATURE [Part::Cut] Cut097
  Base = -> Fillet035
  Tool = -> Cylinder071
FEATURE [Part::Cut] Cut098
  Base = -> Cut097
  Tool = -> Cylinder073
FEATURE [Part::Cut] Cut099  label="Lateral_Iz002"
  Base = -> Cut098
  Tool = -> Cylinder072
FEATURE [Part::Fillet] Fillet039
  Base = -> Box100
  EdgeLinks = -> Box100 [Edge7]
  Edges = 1 edges r=3: [Edge7]
FEATURE [Part::Cut] Cut112
  Base = -> Fillet039
  Tool = -> Cylinder085
FEATURE [Part::Fillet] Fillet040
  Base = -> Box101
  EdgeLinks = -> Box101 [Edge5]
  Edges = 1 edges r=3: [Edge5]
FEATURE [Part::Cut] Cut111
  Base = -> Fillet040
  Tool = -> Cylinder084
FEATURE [Part::Fillet] Fillet041
  Base = -> Cut111
  EdgeLinks = -> Cut111 [Edge15]
  Edges = 1 edges r=0.5: [Edge15]
  Placement = pos=(0,2,0) rot=(0,0,1;0rad)
FEATURE [Part::Fillet] Fillet042
  Base = -> Cut112
  EdgeLinks = -> Cut112 [Edge15]
  Edges = 1 edges r=0.5: [Edge15]
  Placement = pos=(0,2,0) rot=(0,0,1;0rad)
FEATURE [Part::Fillet] Fillet043
  Base = -> Cut116
  EdgeLinks = -> Cut116 [Edge23]
  Edges = 1 edges r=1: [Edge23]
FEATURE [Part::Fillet] Fillet001
  Base = -> Fillet043
  EdgeLinks = -> Fillet043 [Edge4]
  Edges = 1 edges r=1: [Edge4]
FEATURE [Part::Fillet] Fillet002  label="PortaSensor"
  Base = -> Fillet001
  EdgeLinks = -> Fillet001 [Edge34]
  Edges = 1 edges r=1: [Edge34]
  Placement = pos=(-12,11,110) rot=(0,0,1;0rad)
FEATURE [Part::Fillet] Fillet044
  Base = -> Fillet002
  EdgeLinks = -> Fillet002 [Edge48]
  Edges = 1 edges r=1: [Edge48]
FEATURE [Part::Fillet] Fillet045
  Base = -> Fillet044
  EdgeLinks = -> Fillet044 [Edge18]
  Edges = 1 edges r=1: [Edge18]
FEATURE [Part::Fillet] Fillet046
  Base = -> Fillet045
  EdgeLinks = -> Fillet045 [Edge22]
  Edges = 1 edges r=1: [Edge22]
FEATURE [Part::Fillet] Fillet049
  Base = -> Box110
  EdgeLinks = -> Box110 [Edge1,Edge3,Edge5,Edge7]
  Edges = 4 edges r=6: [Edge1,Edge3,Edge5,Edge7]
FEATURE [Part::Fillet] Fillet051
  Base = -> Box111
  EdgeLinks = -> Box111 [Edge1,Edge3]
  Edges = 2 edges r=1.5: [Edge1,Edge3]
FEATURE [Part::Fillet] Fillet052  label="Lateral_Iz006"
  Base = -> Fillet051
  EdgeLinks = -> Fillet051 [Edge17,Edge18]
  Edges = 2 edges r=1.5: [Edge17,Edge18]
FEATURE [Part::Cut] Cut120
  Base = -> Fillet052
  Tool = -> Cylinder086
FEATURE [Part::Cut] Cut121
  Base = -> Cut120
  Tool = -> Cylinder088
FEATURE [Part::Cut] Cut122  label="Lateral_Iz004"
  Base = -> Cut121
  Tool = -> Cylinder087
FEATURE [Part::Fillet] Fillet053
  Base = -> Box114
  EdgeLinks = -> Box114 [Edge1,Edge3]
  Edges = 2 edges r=1.5: [Edge1,Edge3]
FEATURE [Part::Fillet] Fillet054  label="Lateral_De005"
  Base = -> Fillet053
  EdgeLinks = -> Fillet053 [Edge17,Edge18]
  Edges = 2 edges r=1.5: [Edge17,Edge18]
  Placement = pos=(56,0,0) rot=(0,0,1;0rad)
FEATURE [Part::Cut] Cut124
  Base = -> Fillet054
  Tool = -> Cylinder091
FEATURE [Part::Cut] Cut125
  Base = -> Cut124
  Tool = -> Cylinder090
FEATURE [Part::Cut] Cut126
  Base = -> Cut125
  Tool = -> Cylinder089
FEATURE [Part::Fillet] Fillet058
  Base = -> Box118
  EdgeLinks = -> Box118 [Edge7]
  Edges = 1 edges r=3: [Edge7]
FEATURE [Part::Cut] Cut136
  Base = -> Fillet058
  Tool = -> Cylinder103
FEATURE [Part::Fillet] Fillet059
  Base = -> Box119
  EdgeLinks = -> Box119 [Edge5]
  Edges = 1 edges r=3: [Edge5]
FEATURE [Part::Cut] Cut135
  Base = -> Fillet059
  Tool = -> Cylinder102
FEATURE [Part::Fillet] Fillet060
  Base = -> Cut135
  EdgeLinks = -> Cut135 [Edge15]
  Edges = 1 edges r=0.5: [Edge15]
  Placement = pos=(0,2,0) rot=(0,0,1;0rad)
FEATURE [Part::Fillet] Fillet061
  Base = -> Cut136
  EdgeLinks = -> Cut136 [Edge15]
  Edges = 1 edges r=0.5: [Edge15]
  Placement = pos=(0,2,0) rot=(0,0,1;0rad)
FEATURE [Part::Fillet] Fillet062
  Base = -> Box120
  EdgeLinks = -> Box120 [Edge3,Edge7]
  Edges = 2 edges r=1.5: [Edge3,Edge7]
FEATURE [Part::Fillet] Fillet063
  Base = -> Fillet062
  EdgeLinks = -> Fillet062 [Edge2,Edge13]
  Edges = 2 edges r=1.5: [Edge2,Edge13]
  Placement = pos=(0,0,-3) rot=(0,0,1;0rad)
FEATURE [Part::Fillet] Fillet064
  Base = -> Box121
  EdgeLinks = -> Box121 [Edge3,Edge7]
  Edges = 2 edges r=1.5: [Edge3,Edge7]
FEATURE [Part::Fillet] Fillet065
  Base = -> Fillet064
  EdgeLinks = -> Fillet064 [Edge2,Edge13]
  Edges = 2 edges r=1.5: [Edge2,Edge13]
  Placement = pos=(0,0,-3) rot=(0,0,1;0rad)
FEATURE [Part::Fillet] Fillet069
  Base = -> Cut144
  EdgeLinks = -> Cut144 [Edge23]
  Edges = 1 edges r=1: [Edge23]
FEATURE [Part::Fillet] Fillet070
  Base = -> Fillet069
  EdgeLinks = -> Fillet069 [Edge4]
  Edges = 1 edges r=1: [Edge4]
FEATURE [Part::Fillet] Fillet071  label="PortaSensor_Inclinacion002"
  Base = -> Fillet070
  EdgeLinks = -> Fillet070 [Edge34]
  Edges = 1 edges r=1: [Edge34]
  Placement = pos=(0,3.5,4) rot=(0,0,1;0rad)
FEATURE [Part::Fillet] Fillet072
  Base = -> Fillet071
  EdgeLinks = -> Fillet071 [Edge48]
  Edges = 1 edges r=1: [Edge48]
FEATURE [Part::Fillet] Fillet073  label="PortaSensor_TemHum001"
  Base = -> Fillet072
  EdgeLinks = -> Fillet072 [Edge7,Edge18]
  Edges = 2 edges r=1: [Edge7,Edge18]
  Placement = pos=(17.5,13,140) rot=(0.57735,-0.57735,-0.57735;4.18879rad)
FEATURE [Part::Fillet] Fillet081
  Base = -> Cut150
  EdgeLinks = -> Cut150 [Edge23]
  Edges = 1 edges r=1: [Edge23]
FEATURE [Part::Fillet] Fillet082  label="PortaSensor_Inclinación"
  Base = -> Fillet081
  EdgeLinks = -> Fillet081 [Edge8]
  Edges = 1 edges r=1: [Edge8]
  Placement = pos=(-10,-11,110) rot=(1,0,0;1.5708rad)
FEATURE [Part::Fillet] Fillet083
  Base = -> Cut153
  EdgeLinks = -> Cut153 [Edge13,Edge29]
  Edges = 2 edges r=1.5: [Edge13,Edge29]
FEATURE [Part::Fillet] Fillet084  label="PortaPilas_9V"
  Base = -> Fillet083
  EdgeLinks = -> Fillet083 [Edge23,Edge41]
  Edges = 2 edges r=1.5: [Edge23,Edge41]
FEATURE [Part::Fillet] Fillet120
  Base = -> Cylinder134
  EdgeLinks = -> Cylinder134 [Edge3]
  Edges = 1 edges r=1: [Edge3]
FEATURE [Part::Cut] Cut205
  Base = -> Fillet120
  Tool = -> Cylinder136
FEATURE [Part::Cut] Cut206  label="BaseInf010"
  Base = -> Cut205
  Tool = -> Cylinder135
FEATURE [Part::Cut] Cut207  label="BaseInf011"
  Base = -> Cut206
  Tool = -> Cylinder137
FEATURE [Part::Cut] Cut208  label="BaseInf012"
  Base = -> Cut207
  Tool = -> Box170
FEATURE [Part::Fillet] Fillet121
  Base = -> Box171
  EdgeLinks = -> Box171 [Edge1,Edge3,Edge5,Edge7]
  Edges = 4 edges r=2: [Edge1,Edge3,Edge5,Edge7]
  Placement = pos=(33,-4,0) rot=(0,0,1;0rad)
FEATURE [Part::Fillet] Fillet122
  Base = -> Box172
  EdgeLinks = -> Box172 [Edge1,Edge3,Edge5,Edge7]
  Edges = 4 edges r=2: [Edge1,Edge3,Edge5,Edge7]
  Placement = pos=(-39,-4,0) rot=(0,0,1;0rad)
FEATURE [Part::Cut] Cut209
  Base = -> Cut208
  Tool = -> Fillet122
FEATURE [Part::Cut] Cut210  label="BaseInf013"
  Base = -> Cut209
  Tool = -> Fillet121
FEATURE [Part::Fillet] Fillet123
  Base = -> Box173
  EdgeLinks = -> Box173 [Edge1,Edge3]
  Edges = 2 edges r=1.5: [Edge1,Edge3]
FEATURE [Part::Fillet] Fillet124  label="Lateral_Iz010"
  Base = -> Fillet123
  EdgeLinks = -> Fillet123 [Edge17,Edge18]
  Edges = 2 edges r=1.5: [Edge17,Edge18]
FEATURE [Part::Cut] Cut211
  Base = -> Fillet124
  Tool = -> Cylinder138
FEATURE [Part::Cut] Cut212
  Base = -> Cut211
  Tool = -> Cylinder140
FEATURE [Part::Cut] Cut213  label="Lateral_Iz008"
  Base = -> Cut212
  Tool = -> Cylinder139
FEATURE [Part::Fillet] Fillet125
  Base = -> Box176
  EdgeLinks = -> Box176 [Edge1,Edge3]
  Edges = 2 edges r=1.5: [Edge1,Edge3]
FEATURE [Part::Fillet] Fillet126  label="Lateral_De009"
  Base = -> Fillet125
  EdgeLinks = -> Fillet125 [Edge17,Edge18]
  Edges = 2 edges r=1.5: [Edge17,Edge18]
  Placement = pos=(56,0,0) rot=(0,0,1;0rad)
FEATURE [Part::Cut] Cut215
  Base = -> Fillet126
  Tool = -> Cylinder143
FEATURE [Part::Cut] Cut216
  Base = -> Cut215
  Tool = -> Cylinder142
FEATURE [Part::Cut] Cut217
  Base = -> Cut216
  Tool = -> Cylinder141
FEATURE [Part::Fillet] Fillet130
  Base = -> Box180
  EdgeLinks = -> Box180 [Edge7]
  Edges = 1 edges r=3: [Edge7]
FEATURE [Part::Cut] Cut227
  Base = -> Fillet130
  Tool = -> Cylinder155
FEATURE [Part::Fillet] Fillet131
  Base = -> Box181
  EdgeLinks = -> Box181 [Edge5]
  Edges = 1 edges r=3: [Edge5]
FEATURE [Part::Cut] Cut226
  Base = -> Fillet131
  Tool = -> Cylinder154
FEATURE [Part::Fillet] Fillet132
  Base = -> Cut226
  EdgeLinks = -> Cut226 [Edge15]
  Edges = 1 edges r=0.5: [Edge15]
  Placement = pos=(0,2,0) rot=(0,0,1;0rad)
FEATURE [Part::Fillet] Fillet133
  Base = -> Cut227
  EdgeLinks = -> Cut227 [Edge15]
  Edges = 1 edges r=0.5: [Edge15]
  Placement = pos=(0,2,0) rot=(0,0,1;0rad)
FEATURE [Part::Fillet] Fillet134
  Base = -> Box182
  EdgeLinks = -> Box182 [Edge3,Edge7]
  Edges = 2 edges r=1.5: [Edge3,Edge7]
FEATURE [Part::Fillet] Fillet135
  Base = -> Fillet134
  EdgeLinks = -> Fillet134 [Edge2,Edge13]
  Edges = 2 edges r=1.5: [Edge2,Edge13]
  Placement = pos=(0,0,-3) rot=(0,0,1;0rad)
FEATURE [Part::Fillet] Fillet136
  Base = -> Box183
  EdgeLinks = -> Box183 [Edge3,Edge7]
  Edges = 2 edges r=1.5: [Edge3,Edge7]
FEATURE [Part::Fillet] Fillet137
  Base = -> Fillet136
  EdgeLinks = -> Fillet136 [Edge2,Edge13]
  Edges = 2 edges r=1.5: [Edge2,Edge13]
  Placement = pos=(0,0,-3) rot=(0,0,1;0rad)
FEATURE [Part::Fillet] Fillet145
  Base = -> Cylinder162
  EdgeLinks = -> Cylinder162 [Edge3]
  Edges = 1 edges r=0.5: [Edge3]
FEATURE [Part::Fillet] Fillet146
  Base = -> Fillet145
  EdgeLinks = -> Fillet145 [Edge3]
  Edges = 1 edges r=0.5: [Edge3]
FEATURE [Part::Fillet] Fillet147
  Base = -> Cylinder163
  EdgeLinks = -> Cylinder163 [Edge3]
  Edges = 1 edges r=0.5: [Edge3]
FEATURE [Part::Fillet] Fillet148
  Base = -> Fillet147
  EdgeLinks = -> Fillet147 [Edge3]
  Edges = 1 edges r=0.5: [Edge3]
FEATURE [Part::MultiFuse] Fusion069
  Shapes = -> [Cylinder074,Cylinder075]
FEATURE [Part::MultiFuse] Fusion070
  Shapes = -> [Box097,Fusion069]
FEATURE [Part::MultiFuse] Fusion071
  Shapes = -> [Fusion070,Box098]
FEATURE [Part::Cut] Cut103
  Base = -> Fusion071
  Tool = -> Cylinder076
FEATURE [Part::Cut] Cut104  label="Servo002"
  Base = -> Cut103
  Tool = -> Cylinder077
FEATURE [Part::MultiFuse] Fusion072
  Shapes = -> [Cylinder078,Box099]
FEATURE [Part::Fillet] Fillet036
  Base = -> Fusion072
  EdgeLinks = -> Fusion072 [Edge4]
  Edges = 1 edges r=2: [Edge4]
FEATURE [Part::Fillet] Fillet037
  Base = -> Fillet036
  EdgeLinks = -> Fillet036 [Edge25]
  Edges = 1 edges r=1: [Edge25]
FEATURE [Part::Fillet] Fillet038
  Base = -> Fillet037
  EdgeLinks = -> Fillet037 [Edge17]
  Edges = 1 edges r=1: [Edge17]
FEATURE [Part::MultiFuse] Fusion073
  Shapes = -> [Cut104,Fillet038]
FEATURE [Part::Cut] Cut105
  Base = -> Fusion073
  Tool = -> Cylinder079
FEATURE [Part::Cut] Cut106
  Base = -> Cut105
  Tool = -> Cylinder083
FEATURE [Part::Cut] Cut107
  Base = -> Cut106
  Tool = -> Cylinder082
FEATURE [Part::Cut] Cut108
  Base = -> Cut107
  Tool = -> Cylinder081
FEATURE [Part::Cut] Cut109  label="Servo003"
  Base = -> Cut108
  Placement = pos=(41,12,85) rot=(0.707107,-0.707107,0;3.14159rad)
  Tool = -> Cylinder080
FEATURE [Part::Cut] Cut110
  Base = -> Cut102
  Tool = -> Cut109
FEATURE [Part::MultiFuse] Fusion
  Shapes = -> [Cut110,Fillet041]
FEATURE [Part::MultiFuse] Fusion074  label="Lateral_De002"
  Shapes = -> [Fusion,Fillet042]
FEATURE [Part::MultiFuse] Fusion078
  Shapes = -> [Cylinder092,Cylinder093]
FEATURE [Part::MultiFuse] Fusion079
  Shapes = -> [Box115,Fusion078]
FEATURE [Part::MultiFuse] Fusion080
  Shapes = -> [Fusion079,Box116]
FEATURE [Part::Cut] Cut127
  Base = -> Fusion080
  Tool = -> Cylinder094
FEATURE [Part::Cut] Cut128  label="Servo004"
  Base = -> Cut127
  Tool = -> Cylinder095
FEATURE [Part::MultiFuse] Fusion081
  Shapes = -> [Cylinder096,Box117]
FEATURE [Part::Fillet] Fillet055
  Base = -> Fusion081
  EdgeLinks = -> Fusion081 [Edge4]
  Edges = 1 edges r=2: [Edge4]
FEATURE [Part::Fillet] Fillet056
  Base = -> Fillet055
  EdgeLinks = -> Fillet055 [Edge25]
  Edges = 1 edges r=1: [Edge25]
FEATURE [Part::Fillet] Fillet057
  Base = -> Fillet056
  EdgeLinks = -> Fillet056 [Edge17]
  Edges = 1 edges r=1: [Edge17]
FEATURE [Part::MultiFuse] Fusion082
  Shapes = -> [Cut128,Fillet057]
FEATURE [Part::Cut] Cut129
  Base = -> Fusion082
  Tool = -> Cylinder097
FEATURE [Part::Cut] Cut130
  Base = -> Cut129
  Tool = -> Cylinder101
FEATURE [Part::Cut] Cut131
  Base = -> Cut130
  Tool = -> Cylinder100
FEATURE [Part::Cut] Cut132
  Base = -> Cut131
  Tool = -> Cylinder099
FEATURE [Part::Cut] Cut133  label="Servo005"
  Base = -> Cut132
  Placement = pos=(41,12,85) rot=(0.707107,-0.707107,0;3.14159rad)
  Tool = -> Cylinder098
FEATURE [Part::Cut] Cut134
  Base = -> Cut126
  Tool = -> Cut133
FEATURE [Part::MultiFuse] Fusion077
  Shapes = -> [Cut134,Fillet060]
FEATURE [Part::MultiFuse] Fusion083  label="Lateral_De006"
  Shapes = -> [Fusion077,Fillet061]
FEATURE [Part::MultiFuse] Fusion084
  Shapes = -> [Fillet073,Box130]
FEATURE [Part::Fillet] Fillet077
  Base = -> Fusion084
  EdgeLinks = -> Fusion084 [Edge2,Edge16]
  Edges = 2 edges r=1: [Edge2,Edge16]
FEATURE [Part::Fillet] Fillet078  label="PortaSensor_TemHum002"
  Base = -> Fillet077
  EdgeLinks = -> Fillet077 [Edge20,Edge56]
  Edges = 2 edges r=1: [Edge20,Edge56]
FEATURE [Part::Fillet] Fillet079
  Base = -> Fillet078
  EdgeLinks = -> Fillet078 [Edge45]
  Edges = 1 edges r=1.5: [Edge45]
FEATURE [Part::Fillet] Fillet080  label="PortaSensor_TemHum003"
  Base = -> Fillet079
  EdgeLinks = -> Fillet079 [Edge39]
  Edges = 1 edges r=1.5: [Edge39]
  Placement = pos=(1,15.5,0) rot=(0,0,1;0rad)
FEATURE [Part::MultiFuse] Fusion097
  Shapes = -> [Cylinder144,Cylinder145]
FEATURE [Part::MultiFuse] Fusion098
  Shapes = -> [Box177,Fusion097]
FEATURE [Part::MultiFuse] Fusion099
  Shapes = -> [Fusion098,Box178]
FEATURE [Part::Cut] Cut218
  Base = -> Fusion099
  Tool = -> Cylinder146
FEATURE [Part::Cut] Cut219  label="Servo006"
  Base = -> Cut218
  Tool = -> Cylinder147
FEATURE [Part::MultiFuse] Fusion100
  Shapes = -> [Cylinder148,Box179]
FEATURE [Part::Fillet] Fillet127
  Base = -> Fusion100
  EdgeLinks = -> Fusion100 [Edge4]
  Edges = 1 edges r=2: [Edge4]
FEATURE [Part::Fillet] Fillet128
  Base = -> Fillet127
  EdgeLinks = -> Fillet127 [Edge25]
  Edges = 1 edges r=1: [Edge25]
FEATURE [Part::Fillet] Fillet129
  Base = -> Fillet128
  EdgeLinks = -> Fillet128 [Edge17]
  Edges = 1 edges r=1: [Edge17]
FEATURE [Part::MultiFuse] Fusion101
  Shapes = -> [Cut219,Fillet129]
FEATURE [Part::Cut] Cut220
  Base = -> Fusion101
  Tool = -> Cylinder149
FEATURE [Part::Cut] Cut221
  Base = -> Cut220
  Tool = -> Cylinder153
FEATURE [Part::Cut] Cut222
  Base = -> Cut221
  Tool = -> Cylinder152
FEATURE [Part::Cut] Cut223
  Base = -> Cut222
  Tool = -> Cylinder151
FEATURE [Part::Cut] Cut224  label="Servo007"
  Base = -> Cut223
  Placement = pos=(41,12,85) rot=(0.707107,-0.707107,0;3.14159rad)
  Tool = -> Cylinder150
FEATURE [Part::Cut] Cut225
  Base = -> Cut217
  Tool = -> Cut224
FEATURE [Part::MultiFuse] Fusion096
  Shapes = -> [Cut225,Fillet132]
FEATURE [Part::MultiFuse] Fusion102  label="Lateral_De010"
  Shapes = -> [Fusion096,Fillet133]
FEATURE [Part::Offset] Offset
  Fill = false
  Intersection = false
  Join = 0
  Mode = 0
  SelfIntersection = false
  Source = -> Fillet011
  Value = 0.2
FEATURE [Part::Cut] Cut004
  Base = -> Cut003
  Tool = -> Offset
FEATURE [Part::Offset] Offset001
  Fill = false
  Intersection = false
  Join = 0
  Mode = 0
  SelfIntersection = false
  Source = -> Fillet013
  Value = 0.2
FEATURE [Part::Cut] Cut005  label="Base_2"
  Base = -> Cut004
  Placement = pos=(0,0,10) rot=(0,0,1;0rad)
  Tool = -> Offset001
FEATURE [Part::Cut] Cut012
  Base = -> Cut005
  Tool = -> Fillet019
FEATURE [Part::Cut] Cut013
  Base = -> Cut012
  Tool = -> Fillet022
FEATURE [Part::MultiFuse] Fusion002  label="BaseSup"
  Shapes = -> [Cut013,Cut017]
FEATURE [Part::MultiFuse] Fusion075  label="BaseSup001"
  Shapes = -> [Fusion002,Fillet046]
FEATURE [Part::Fillet] Fillet047
  Base = -> Fusion075
  EdgeLinks = -> Fusion075 [Edge125]
  Edges = 1 edges r=2: [Edge125]
FEATURE [Part::Fillet] Fillet048
  Base = -> Fillet047
  EdgeLinks = -> Fillet047 [Edge136]
  Edges = 1 edges r=2: [Edge136]
FEATURE [Part::MultiFuse] Fusion076
  Shapes = -> [Fillet048,Fillet007]
FEATURE [Part::Chamfer] Chamfer  label="BaseSup002"
  Base = -> Fusion076
  EdgeLinks = -> Fusion076 [Edge137]
  Edges = 1 edges r=2: [Edge137]
FEATURE [Part::Cut] Cut119
  Base = -> Chamfer
  Tool = -> Fillet049
FEATURE [Part::Fillet] Fillet050  label="BaseSup003"
  Base = -> Cut119
  EdgeLinks = -> Cut119 [Edge41,Edge45]
  Edges = 2 edges r=1: [Edge41,Edge45]
FEATURE [Part::Cut] Cut147  label="BaseInf007"
  Base = -> Fillet050
  Tool = -> Box128
FEATURE [Part::Cut] Cut148
  Base = -> Cut147
  Tool = -> Box129
FEATURE [Part::Cut] Cut151  label="BaseSup004"
  Base = -> Cut148
  Tool = -> Box134
FEATURE [Part::MultiFuse] Fusion085
  Shapes = -> [Cut151,Fillet084]
FEATURE [Part::MultiFuse] Fusion086
  Shapes = -> [Fusion085,Fillet082]
FEATURE [Part::MultiFuse] Fusion087  label="BaseSup005"
  Shapes = -> [Fusion086,Fillet080]
FEATURE [Part::Cut] Cut235
  Base = -> Fusion087
  Tool = -> Box184
FEATURE [Part::Fillet] Fillet141
  Base = -> Cut235
  EdgeLinks = -> Cut235 [Edge15]
  Edges = 1 edges r=2.5: [Edge15]
FEATURE [Part::Fillet] Fillet142
  Base = -> Fillet141
  EdgeLinks = -> Fillet141 [Edge97]
  Edges = 1 edges r=2.5: [Edge97]
FEATURE [Part::Fillet] Fillet143
  Base = -> Fillet142
  EdgeLinks = -> Fillet142 [Edge20]
  Edges = 1 edges r=2.5: [Edge20]
FEATURE [Part::Fillet] Fillet144  label="BloquComponentes"
  Base = -> Fillet143
  EdgeLinks = -> Fillet143 [Edge92]
  Edges = 1 edges r=2.5: [Edge92]
FEATURE [Part::MultiFuse] Fusion103
  Shapes = -> [Fillet144,Cylinder158]
FEATURE [Part::MultiFuse] Fusion104
  Shapes = -> [Fusion103,Cylinder161]
FEATURE [Part::MultiFuse] Fusion105
  Shapes = -> [Fusion104,Cylinder160]
FEATURE [Part::MultiFuse] Fusion106
  Shapes = -> [Fusion105,Cylinder159]
FEATURE [Part::MultiFuse] Fusion107
  Shapes = -> [Fusion106,Fillet146]
FEATURE [Part::MultiFuse] Fusion108
  Shapes = -> [Fusion107,Fillet148]
FEATURE [Part::Offset] Offset002
  Fill = false
  Intersection = false
  Join = 0
  Mode = 0
  SelfIntersection = false
  Source = -> Box
  Value = 0.2
FEATURE [Part::Cut] Cut114  label="Lateral_De003"
  Base = -> Fusion074
  Tool = -> Offset002
FEATURE [Part::Cut] Cut177
  Base = -> Cut114
  Tool = -> Box165
FEATURE [Part::Cut] Cut179
  Base = -> Cut177
  Tool = -> Box167
FEATURE [Part::Cut] Cut181
  Base = -> Cut179
  Tool = -> Cylinder110
FEATURE [Part::Cut] Cut182
  Base = -> Cut181
  Tool = -> Cylinder111
FEATURE [Part::Cut] Cut183
  Base = -> Cut182
  Tool = -> Cylinder112
FEATURE [Part::Cut] Cut184
  Base = -> Cut183
  Tool = -> Cylinder120
FEATURE [Part::Cut] Cut185
  Base = -> Cut184
  Tool = -> Cylinder119
FEATURE [Part::Cut] Cut186
  Base = -> Cut185
  Tool = -> Cylinder118
FEATURE [Part::Cut] Cut187
  Base = -> Cut186
  Tool = -> Cylinder117
FEATURE [Part::Cut] Cut188
  Base = -> Cut187
  Tool = -> Cylinder116
FEATURE [Part::Cut] Cut189
  Base = -> Cut188
  Tool = -> Cylinder115
FEATURE [Part::Cut] Cut190
  Base = -> Cut189
  Tool = -> Cylinder114
FEATURE [Part::Cut] Cut191  label="LateralDer"
  Base = -> Cut190
  Tool = -> Cylinder113
FEATURE [Part::Cut] Cut202
  Base = -> Cut191
  Tool = -> Box168
FEATURE [Part::Cut] Cut203  label="LateralDer001"
  Base = -> Cut202
  Tool = -> Box169
FEATURE [Part::Cut] Cut255  label="LateralDer002"
  Base = -> Cut203
  Tool = -> Box197
FEATURE [Part::Cut] Cut256  label="LateralDer003"
  Base = -> Cut255
  Tool = -> Box198
FEATURE [Part::Offset] Offset003
  Fill = false
  Intersection = false
  Join = 0
  Mode = 0
  SelfIntersection = false
  Source = -> Box102
  Value = 0.2
FEATURE [Part::Cut] Cut113  label="Lateral_Iz003"
  Base = -> Cut099
  Tool = -> Offset003
FEATURE [Part::Cut] Cut178
  Base = -> Cut113
  Tool = -> Box166
FEATURE [Part::Cut] Cut180
  Base = -> Cut178
  Tool = -> Cylinder109
FEATURE [Part::Cut] Cut192
  Base = -> Cut180
  Tool = -> Cylinder121
FEATURE [Part::Cut] Cut193
  Base = -> Cut192
  Tool = -> Cylinder130
FEATURE [Part::Cut] Cut194
  Base = -> Cut193
  Tool = -> Cylinder129
FEATURE [Part::MultiFuse] Fusion095
  Shapes = -> [Cut194,Cylinder128]
FEATURE [Part::Cut] Cut195
  Base = -> Fusion095
  Tool = -> Cylinder127
FEATURE [Part::Cut] Cut196
  Base = -> Cut195
  Tool = -> Cylinder126
FEATURE [Part::Cut] Cut197
  Base = -> Cut196
  Tool = -> Cylinder125
FEATURE [Part::Cut] Cut198
  Base = -> Cut197
  Tool = -> Cylinder124
FEATURE [Part::Cut] Cut199
  Base = -> Cut198
  Tool = -> Cylinder123
FEATURE [Part::Cut] Cut200
  Base = -> Cut199
  Tool = -> Cylinder122
FEATURE [Part::Cut] Cut201  label="LateralIzq"
  Base = -> Cut200
  Tool = -> Cylinder131
FEATURE [Part::Offset] Offset004
  Fill = false
  Intersection = false
  Join = 0
  Mode = 0
  SelfIntersection = false
  Source = -> Box112
  Value = 0.2
FEATURE [Part::Cut] Cut123  label="Lateral_Iz005"
  Base = -> Cut122
  Tool = -> Offset004
FEATURE [Part::Cut] Cut138
  Base = -> Cut096
  Tool = -> Cut123
FEATURE [Part::Offset] Offset005
  Fill = false
  Intersection = false
  Join = 0
  Mode = 0
  SelfIntersection = false
  Source = -> Box113
  Value = 0.2
FEATURE [Part::Cut] Cut137  label="Lateral_De004"
  Base = -> Fusion083
  Tool = -> Offset005
FEATURE [Part::Cut] Cut139  label="BaseInf004"
  Base = -> Cut138
  Tool = -> Cut137
FEATURE [Part::Offset] Offset006
  Fill = false
  Intersection = false
  Join = 0
  Mode = 0
  SelfIntersection = false
  Source = -> Fillet063
  Value = 0.2
FEATURE [Part::Cut] Cut140
  Base = -> Cut139
  Tool = -> Offset006
FEATURE [Part::Offset] Offset007
  Fill = false
  Intersection = false
  Join = 0
  Mode = 0
  Placement = pos=(56,0,0) rot=(0,0,1;0rad)
  SelfIntersection = false
  Source = -> Fillet065
  Value = 0.2
FEATURE [Part::Cut] Cut141
  Base = -> Cut140
  Tool = -> Offset007
FEATURE [Part::Fillet] Fillet066
  Base = -> Cut141
  EdgeLinks = -> Cut141 [Edge55,Edge56,Edge57,Edge58,Edge59,Edge60,Edge61]
  Edges = 7 edges r=1: [Edge55,Edge56,Edge57,Edge58,Edge59,Edge60,Edge61]
FEATURE [Part::Fillet] Fillet067
  Base = -> Fillet066
  EdgeLinks = -> Fillet066 [Edge34,Edge38]
  Edges = 2 edges r=1: [Edge34,Edge38]
FEATURE [Part::Fillet] Fillet068  label="BaseInf005"
  Base = -> Fillet067
  EdgeLinks = -> Fillet067 [Edge28,Edge32]
  Edges = 2 edges r=1: [Edge28,Edge32]
FEATURE [Part::Cut] Cut142  label="BaseInf006"
  Base = -> Fillet068
  Tool = -> Cylinder104
FEATURE [Part::Cut] Cut204  label="BaseInf009"
  Base = -> Cut142
  Tool = -> Cylinder133
FEATURE [Part::Offset] Offset010
  Fill = false
  Intersection = false
  Join = 0
  Mode = 0
  SelfIntersection = false
  Source = -> Box174
  Value = 0.2
FEATURE [Part::Cut] Cut214  label="Lateral_Iz009"
  Base = -> Cut213
  Tool = -> Offset010
FEATURE [Part::Cut] Cut229
  Base = -> Cut210
  Tool = -> Cut214
FEATURE [Part::Offset] Offset011
  Fill = false
  Intersection = false
  Join = 0
  Mode = 0
  SelfIntersection = false
  Source = -> Box175
  Value = 0.2
FEATURE [Part::Cut] Cut228  label="Lateral_De008"
  Base = -> Fusion102
  Tool = -> Offset011
FEATURE [Part::Cut] Cut230  label="BaseInf014"
  Base = -> Cut229
  Tool = -> Cut228
FEATURE [Part::Offset] Offset012
  Fill = false
  Intersection = false
  Join = 0
  Mode = 0
  SelfIntersection = false
  Source = -> Fillet135
  Value = 0.2
FEATURE [Part::Cut] Cut231
  Base = -> Cut230
  Tool = -> Offset012
FEATURE [Part::Offset] Offset013
  Fill = false
  Intersection = false
  Join = 0
  Mode = 0
  Placement = pos=(56,0,0) rot=(0,0,1;0rad)
  SelfIntersection = false
  Source = -> Fillet137
  Value = 0.2
FEATURE [Part::Cut] Cut232
  Base = -> Cut231
  Tool = -> Offset013
FEATURE [Part::Fillet] Fillet138
  Base = -> Cut232
  EdgeLinks = -> Cut232 [Edge55,Edge56,Edge57,Edge58,Edge59,Edge60,Edge61]
  Edges = 7 edges r=1: [Edge55,Edge56,Edge57,Edge58,Edge59,Edge60,Edge61]
FEATURE [Part::Fillet] Fillet139
  Base = -> Fillet138
  EdgeLinks = -> Fillet138 [Edge34,Edge38]
  Edges = 2 edges r=1: [Edge34,Edge38]
FEATURE [Part::Fillet] Fillet140  label="BaseInf017"
  Base = -> Fillet139
  EdgeLinks = -> Fillet139 [Edge28,Edge32]
  Edges = 2 edges r=1: [Edge28,Edge32]
FEATURE [Part::Cut] Cut233  label="BaseInf015"
  Base = -> Fillet140
  Tool = -> Cylinder156
FEATURE [Part::Cut] Cut234  label="BaseSup012"
  Base = -> Cut233
  Placement = pos=(0,0,105) rot=(0,0,1;0rad)
  Tool = -> Cylinder157
FEATURE [Part::MultiFuse] Fusion109  label="BaseSup013"
  Shapes = -> [Cut234,Fusion108]
FEATURE [Part::MultiFuse] Fusion178  label="Capsula_Paracaidas"
  Shapes = -> [Cut201,Cut204,Fusion109,Cut256]
